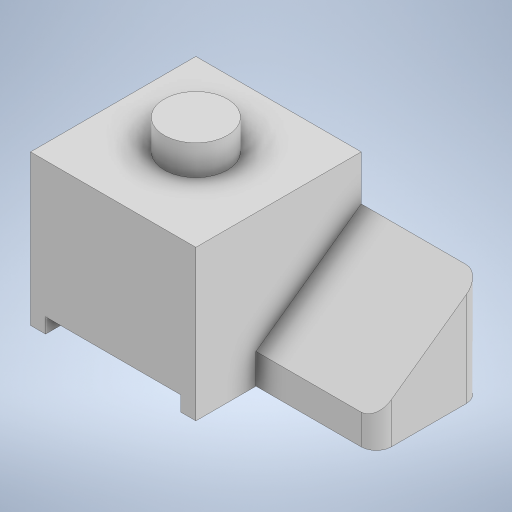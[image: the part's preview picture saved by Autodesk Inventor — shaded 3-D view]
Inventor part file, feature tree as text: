
AUTODESK INVENTOR PART (.ipt)
format: ipt  version: 2024 (Build 280153000, 153)  size: 241,152 bytes
history: native  units: mm
features: extrude x3, sketch x3, fillet x2
ambient origin geometry x8: Origin, YZ Plane, XZ Plane, XY Plane, X Axis, Y Axis, Z Axis, Center Point
bodies: Solid1 (feature_tree)
feature tree (8):
  extrude  "Extrusion1"  Depth=5.0mm
  extrude  "Extrusion2"  Depth=5.0mm
  extrude  "Extrusion3"  Depth=55.0mm TaperAngle=0.0deg
  fillet  "Fillet1"  Radius=21.0mm
  fillet  "Fillet2"  Radius=27.5mm
  sketch  "Sketch1"  dims[d0=50.0mm d1=5.0mm]
  sketch  "Sketch2"  dims[d2=5.0mm d3=5.0mm]
  sketch  "Sketch3"  dims[d4=45.0mm d5=55.0mm d6=0.0mm d7=21.0mm d8=27.5mm d9=27.5mm d10=10.0mm d11=0.0mm d12=35.0mm d13=0.0mm d14=10.0mm d15=35.0mm d16=40.0mm d17=0.0mm d18=5.0mm d19=5.0mm]
